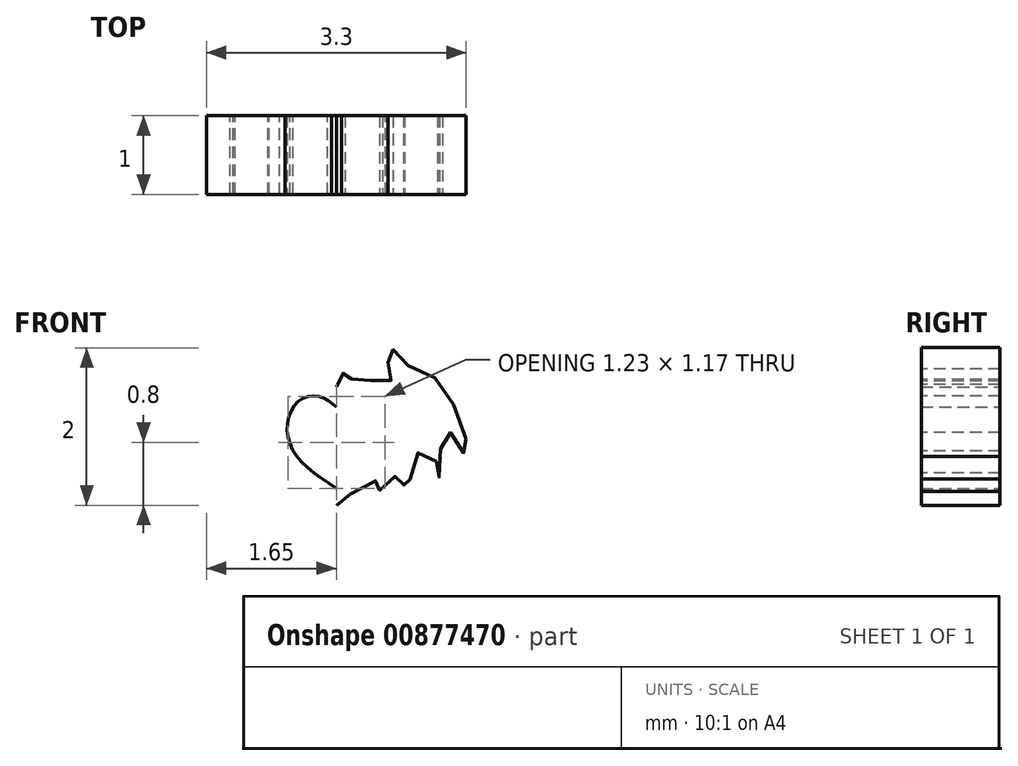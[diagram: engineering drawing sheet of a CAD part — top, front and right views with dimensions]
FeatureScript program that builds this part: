
annotation { "Feature Type Name" : "Feature", "Feature Type Description" : "" }
export const myFeature = defineFeature(function(context is Context, id is Id, definition is map)
    precondition{}
    {
        {
            var Q0;
            Q0=qCreatedBy(makeId("Front.planeOp"),FACE);
            var sketch = newSketch(context, id + "F0", { "sketchPlane" : qUnion([Q0])});
            skFitSpline(sketch, "E0", {"points": [v(0, 1.5) * mm, v(-0.1, 1.56) * mm, v(-0.06, 1.73) * mm, v(-0.22, 1.59) * mm, v(-0.38, 1.6) * mm, v(-0.61, 1.54) * mm, v(-0.72, 1.66) * mm, v(-0.65, 1.82) * mm, v(-0.72, 2) * mm, v(-0.75, 1.86) * mm, v(-1.1, 1.72) * mm, v(-1.39, 1.44) * mm, v(-1.64, 0.9) * mm, v(-1.63, 0.62) * mm, v(-1.54, 0.9) * mm, v(-1.32, 0.84) * mm, v(-1.35, 0.6) * mm, v(-1.3, 0.33) * mm, v(-1.26, 0.58) * mm, v(-1.06, 0.68) * mm, v(-0.98, 0.45) * mm, v(-0.85, 0.18) * mm, v(-0.86, 0.4) * mm, v(-0.71, 0.34) * mm, v(-0.55, 0.18) * mm, v(-0.58, 0.33) * mm, v(-0.32, 0.2) * mm, v(-0.1, 0.12) * mm, v(0, 0) * mm], "startDerivative": vector(-5.94, 0.83) * mm, "endDerivative": vector(3.4, -4.5) * mm});
            skFitSpline(sketch, "E1.MirrorCS", {"points": [v(0, 1.5) * mm, v(0.1, 1.56) * mm, v(0.06, 1.73) * mm, v(0.22, 1.59) * mm, v(0.38, 1.6) * mm, v(0.61, 1.54) * mm, v(0.72, 1.66) * mm, v(0.65, 1.82) * mm, v(0.72, 2) * mm, v(0.75, 1.86) * mm, v(1.1, 1.72) * mm, v(1.39, 1.44) * mm, v(1.64, 0.9) * mm, v(1.63, 0.62) * mm, v(1.54, 0.9) * mm, v(1.32, 0.84) * mm, v(1.35, 0.6) * mm, v(1.3, 0.33) * mm, v(1.26, 0.58) * mm, v(1.06, 0.68) * mm, v(0.98, 0.45) * mm, v(0.85, 0.18) * mm, v(0.86, 0.4) * mm, v(0.71, 0.34) * mm, v(0.55, 0.18) * mm, v(0.58, 0.33) * mm, v(0.32, 0.2) * mm, v(0.1, 0.12) * mm, v(0, 0) * mm], "startDerivative": vector(5.94, 0.83) * mm, "endDerivative": vector(-3.4, -4.5) * mm});
            skFitSpline(sketch, "E2", {"points": [v(0, 1.25) * mm, v(0.2, 1.38) * mm, v(0.47, 1.33) * mm, v(0.62, 1.03) * mm, v(0.51, 0.64) * mm, v(0, 0.22) * mm], "startDerivative": vector(1.16, 1.01) * mm, "endDerivative": vector(-2.24, -1.49) * mm});
            skFitSpline(sketch, "E3.MirrorCS", {"points": [v(0, 1.25) * mm, v(-0.2, 1.38) * mm, v(-0.47, 1.33) * mm, v(-0.62, 1.03) * mm, v(-0.51, 0.64) * mm, v(0, 0.22) * mm], "startDerivative": vector(-1.16, 1.01) * mm, "endDerivative": vector(2.24, -1.49) * mm});
            skSolve(sketch);
        }
        {
            var Q0;
            Q0=makeQuery(id+"F0.imprint","IMPRINT",FACE,{"disambiguationData":[TD([[makeQuery(id+"F0.imprint","IMPRINT",EDGE,{"derivedFrom":sQuery(id+"F0.wireOp",EDGE,"E0")}),1.0]])]});
            extrude(context, id + "F1", {"entities" : qUnion([Q0]), "depth" : 1 * mm, "offsetDistance" : 25 * mm});
        }
    });
